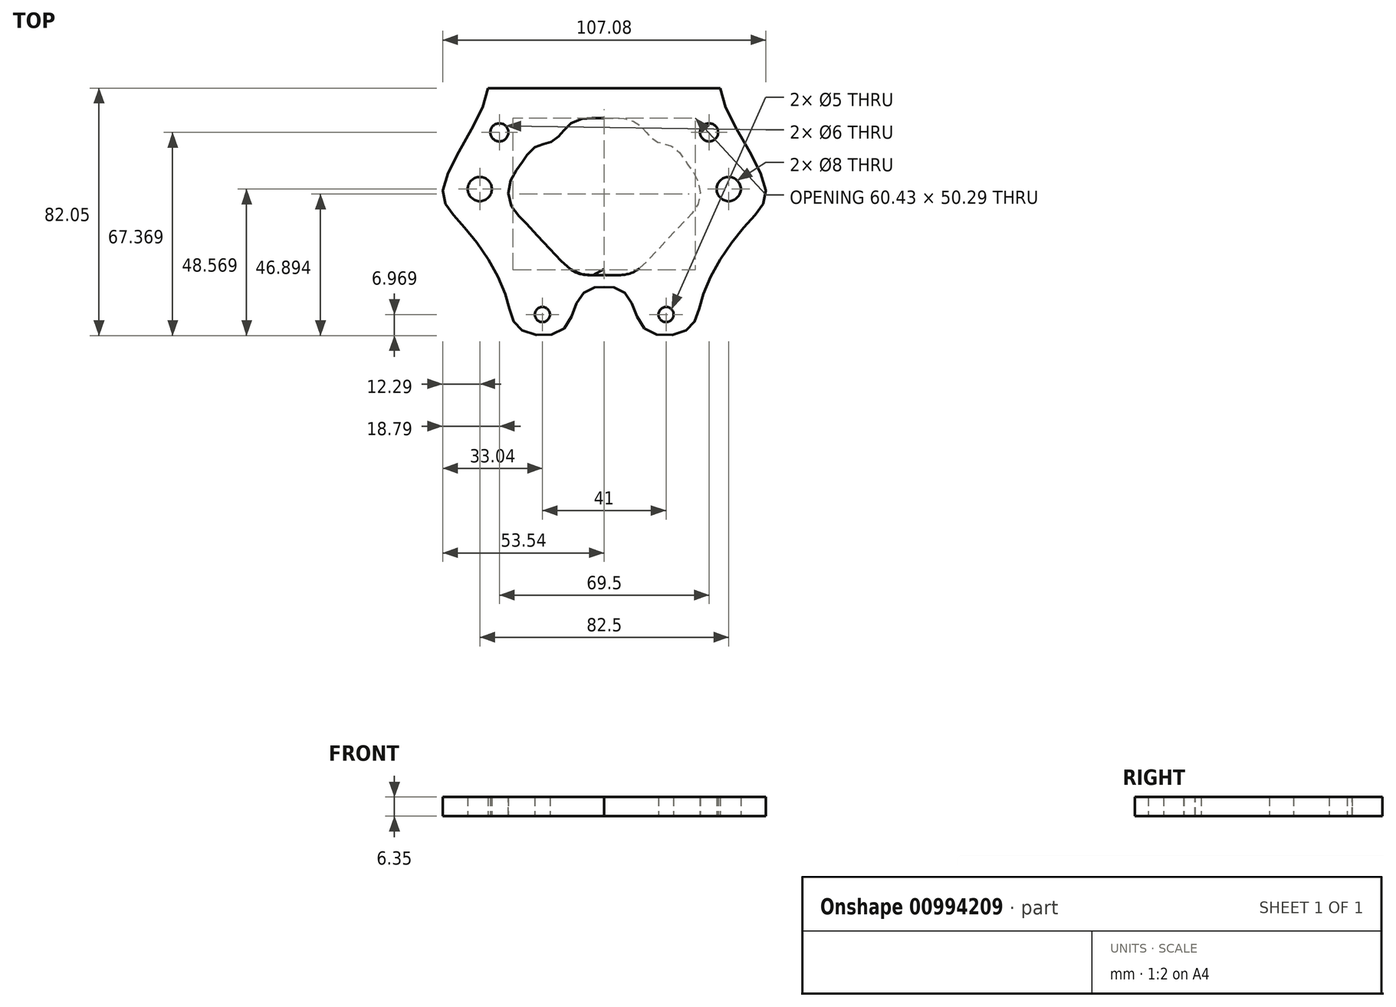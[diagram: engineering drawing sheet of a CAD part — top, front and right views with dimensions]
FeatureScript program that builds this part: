
annotation { "Feature Type Name" : "Feature", "Feature Type Description" : "" }
export const myFeature = defineFeature(function(context is Context, id is Id, definition is map)
    precondition{}
    {
        {
            var Q0;
            Q0=qCreatedBy(makeId("Top.planeOp"),FACE);
            var sketch = newSketch(context, id + "F0", { "sketchPlane" : qUnion([Q0])});
            skCircle(sketch, "E0", {"center": v(-20.5, -31.97) * mm, "radius": 2.5 * mm});
            skCircle(sketch, "E1", {"center": v(20.5, -31.97) * mm, "radius": 2.5 * mm});
            skLineSegment(sketch, "E2", {"start": v(-20.5, -31.97) * mm, "end": v(20.5, -31.97) * mm, "construction": true});
            skPoint(sketch, "E3", {"position": v(0, -31.97) * mm});
            skCircle(sketch, "E4", {"center": v(-20.5, 31.53) * mm, "radius": 2.5 * mm});
            skCircle(sketch, "E5", {"center": v(20.5, 31.53) * mm, "radius": 2.5 * mm});
            skLineSegment(sketch, "E6", {"start": v(-20.5, 31.53) * mm, "end": v(-20.5, -31.97) * mm, "construction": true});
            skLineSegment(sketch, "E7", {"start": v(20.5, 31.53) * mm, "end": v(20.5, -31.97) * mm, "construction": true});
            skLineSegment(sketch, "E8", {"start": v(-20.5, 31.53) * mm, "end": v(20.5, 31.53) * mm, "construction": true});
            skCircle(sketch, "E9", {"center": v(-34.75, 28.43) * mm, "radius": 3 * mm});
            skCircle(sketch, "E10", {"center": v(34.75, 28.43) * mm, "radius": 3 * mm});
            skLineSegment(sketch, "E11", {"start": v(-34.75, 28.43) * mm, "end": v(34.75, 28.43) * mm, "construction": true});
            skPoint(sketch, "E12", {"position": v(0, 28.43) * mm});
            skCircle(sketch, "E13", {"center": v(-41.25, 9.63) * mm, "radius": 4 * mm});
            skCircle(sketch, "E14", {"center": v(41.25, 9.63) * mm, "radius": 4 * mm});
            skLineSegment(sketch, "E15", {"start": v(-41.25, 9.63) * mm, "end": v(41.25, 9.63) * mm, "construction": true});
            skPoint(sketch, "E16", {"position": v(0, 9.63) * mm});
            skSolve(sketch);
        }
        {
            var Q0;
            Q0=qCreatedBy(makeId("Top.planeOp"),FACE);
            var sketch = newSketch(context, id + "F1", { "sketchPlane" : qUnion([Q0])});
            skPoint(sketch, "E17", {"position": v(0, 43.1) * mm});
            skPoint(sketch, "E18", {"position": v(-38.47, 43.1) * mm});
            skFitSpline(sketch, "E19", {"points": [v(-38.47, 43.1) * mm, v(-53.4, 10.03) * mm, v(-46.94, -2.29) * mm, v(-32.99, -24.7) * mm, v(-27.74, -36.86) * mm, v(-13.8, -37.01) * mm, v(-7.55, -25.5) * mm, v(0, -22.83) * mm], "startDerivative": vector(-10.62, -131.68) * mm, "endDerivative": vector(61.34, -11.47) * mm});
            skLineSegment(sketch, "E20", {"start": v(-38.47, 43.1) * mm, "end": v(0, 43.1) * mm});
            skPoint(sketch, "E21.MirrorP", {"position": v(38.47, 43.1) * mm});
            skFitSpline(sketch, "E22.MirrorCS", {"points": [v(38.47, 43.1) * mm, v(53.4, 10.03) * mm, v(46.94, -2.29) * mm, v(32.99, -24.7) * mm, v(27.74, -36.86) * mm, v(13.8, -37.01) * mm, v(7.55, -25.5) * mm, v(0, -22.83) * mm], "startDerivative": vector(10.62, -131.68) * mm, "endDerivative": vector(-61.34, -11.47) * mm});
            skLineSegment(sketch, "E23.MirrorCS", {"start": v(38.47, 43.1) * mm, "end": v(0, 43.1) * mm});
            skCircle(sketch, "E24", {"center": v(-20.5, -31.97) * mm, "radius": 2.5 * mm});
            skCircle(sketch, "E25", {"center": v(20.5, -31.97) * mm, "radius": 2.5 * mm});
            skLineSegment(sketch, "E26", {"start": v(-20.5, -31.97) * mm, "end": v(20.5, -31.97) * mm, "construction": true});
            skPoint(sketch, "E27", {"position": v(0, -31.97) * mm});
            skLineSegment(sketch, "E28", {"start": v(-20.5, 31.53) * mm, "end": v(-20.5, -31.97) * mm, "construction": true});
            skLineSegment(sketch, "E29", {"start": v(20.5, 31.53) * mm, "end": v(20.5, -31.97) * mm, "construction": true});
            skCircle(sketch, "E30", {"center": v(-34.75, 28.43) * mm, "radius": 3 * mm});
            skCircle(sketch, "E31", {"center": v(34.75, 28.43) * mm, "radius": 3 * mm});
            skLineSegment(sketch, "E32", {"start": v(-34.75, 28.43) * mm, "end": v(34.75, 28.43) * mm, "construction": true});
            skPoint(sketch, "E33", {"position": v(0, 28.43) * mm});
            skCircle(sketch, "E34", {"center": v(-41.25, 9.63) * mm, "radius": 4 * mm});
            skCircle(sketch, "E35", {"center": v(41.25, 9.63) * mm, "radius": 4 * mm});
            skLineSegment(sketch, "E36", {"start": v(-41.25, 9.63) * mm, "end": v(41.25, 9.63) * mm, "construction": true});
            skPoint(sketch, "E37", {"position": v(0, 9.63) * mm});
            skFitSpline(sketch, "E38", {"points": [v(0, 28.1) * mm, v(-5.93, 28.05) * mm, v(-8.65, 26.95) * mm, v(-10.13, 25.17) * mm, v(-15.35, 20.78) * mm, v(-20.02, 19.42) * mm, v(-21.23, 18.41) * mm, v(-23.17, 15.5) * mm, v(-26.37, 10.58) * mm, v(-26.53, 6.66) * mm, v(-24.05, 3.5) * mm, v(-16.13, -4.85) * mm, v(-9.1, -12.26) * mm, v(-6.02, -13.8) * mm, v(0, -14.01) * mm], "startDerivative": vector(-72.46, 0) * mm, "endDerivative": vector(69.37, -4.39) * mm});
            skFitSpline(sketch, "E39.MirrorCS", {"points": [v(0, 28.1) * mm, v(5.93, 28.05) * mm, v(8.65, 26.95) * mm, v(10.13, 25.17) * mm, v(15.35, 20.78) * mm, v(20.02, 19.42) * mm, v(21.23, 18.41) * mm, v(23.17, 15.5) * mm, v(26.37, 10.58) * mm, v(26.53, 6.66) * mm, v(24.05, 3.5) * mm, v(16.13, -4.85) * mm, v(9.1, -12.26) * mm, v(6.02, -13.8) * mm, v(0, -14.01) * mm], "startDerivative": vector(72.46, 0) * mm, "endDerivative": vector(-69.37, -4.39) * mm});
            skFitSpline(sketch, "E40.0", {"points": [v(0, 33.1) * mm, v(-0.3, 33.1) * mm, v(-1.01, 33.11) * mm, v(-2.24, 33.15) * mm, v(-3.36, 33.18) * mm, v(-4.3, 33.17) * mm, v(-5.04, 33.15) * mm, v(-5.67, 33.1) * mm, v(-6.2, 33.05) * mm, v(-6.6, 33) * mm, v(-7, 32.94) * mm, v(-7.54, 32.84) * mm, v(-8.2, 32.68) * mm, v(-8.96, 32.43) * mm, v(-9.7, 32.14) * mm, v(-10.42, 31.78) * mm, v(-11.11, 31.36) * mm, v(-11.66, 30.95) * mm, v(-12.08, 30.6) * mm, v(-12.46, 30.23) * mm, v(-12.87, 29.8) * mm, v(-13.24, 29.33) * mm, v(-13.52, 28.96) * mm, v(-13.74, 28.67) * mm, v(-13.9, 28.45) * mm, v(-14.03, 28.3) * mm, v(-14.17, 28.12) * mm, v(-14.38, 27.87) * mm, v(-14.77, 27.45) * mm, v(-15.34, 26.87) * mm, v(-15.96, 26.32) * mm, v(-16.45, 25.94) * mm, v(-16.81, 25.69) * mm, v(-17.14, 25.48) * mm, v(-17.39, 25.34) * mm, v(-17.55, 25.27) * mm, v(-17.68, 25.21) * mm, v(-17.82, 25.16) * mm, v(-18.03, 25.08) * mm, v(-18.31, 25) * mm, v(-18.7, 24.9) * mm, v(-19.14, 24.8) * mm, v(-19.61, 24.69) * mm, v(-20.14, 24.57) * mm, v(-20.65, 24.46) * mm, v(-21.1, 24.33) * mm, v(-21.42, 24.23) * mm, v(-21.69, 24.14) * mm, v(-21.98, 24.02) * mm, v(-22.49, 23.8) * mm, v(-23.23, 23.4) * mm, v(-24.02, 22.79) * mm, v(-24.64, 22.16) * mm, v(-25.02, 21.7) * mm, v(-25.25, 21.4) * mm, v(-25.44, 21.12) * mm, v(-25.67, 20.78) * mm, v(-25.93, 20.4) * mm, v(-26.17, 20.02) * mm, v(-26.4, 19.65) * mm, v(-26.65, 19.28) * mm, v(-26.9, 18.9) * mm, v(-27.1, 18.6) * mm, v(-27.28, 18.36) * mm, v(-27.47, 18.1) * mm, v(-27.73, 17.75) * mm, v(-28.08, 17.28) * mm, v(-28.59, 16.6) * mm, v(-29.14, 15.84) * mm, v(-29.7, 15) * mm, v(-30.11, 14.3) * mm, v(-30.52, 13.56) * mm, v(-30.84, 12.89) * mm, v(-31.07, 12.3) * mm, v(-31.28, 11.71) * mm, v(-31.5, 10.96) * mm, v(-31.69, 10.05) * mm, v(-31.84, 8.83) * mm, v(-31.83, 7.6) * mm, v(-31.64, 6.36) * mm, v(-31.42, 5.45) * mm, v(-31.09, 4.54) * mm, v(-30.68, 3.7) * mm, v(-30.22, 2.95) * mm, v(-29.6, 2.09) * mm, v(-28.97, 1.39) * mm, v(-28.39, 0.78) * mm, v(-28.03, 0.42) * mm, v(-27.75, 0.14) * mm, v(-27.47, -0.14) * mm, v(-27.11, -0.5) * mm, v(-26.64, -0.98) * mm, v(-25.99, -1.65) * mm, v(-25.1, -2.57) * mm, v(-23.98, -3.75) * mm, v(-22.8, -5) * mm, v(-21.6, -6.3) * mm, v(-20.38, -7.6) * mm, v(-19.18, -8.93) * mm, v(-17.98, -10.25) * mm, v(-16.8, -11.53) * mm, v(-15.67, -12.77) * mm, v(-14.57, -13.93) * mm, v(-13.68, -14.82) * mm, v(-12.98, -15.48) * mm, v(-12.46, -15.96) * mm, v(-11.92, -16.41) * mm, v(-11.34, -16.87) * mm, v(-10.68, -17.32) * mm, v(-9.95, -17.74) * mm, v(-9.15, -18.1) * mm, v(-8.32, -18.4) * mm, v(-7.63, -18.58) * mm, v(-7.08, -18.7) * mm, v(-6.54, -18.78) * mm, v(-5.89, -18.86) * mm, v(-4.9, -18.93) * mm, v(-3.71, -18.96) * mm, v(-2.38, -18.96) * mm, v(-1.2, -18.97) * mm, v(-0.56, -18.99) * mm, v(-0.32, -19) * mm, v(0, 33.1) * mm]});
            skFitSpline(sketch, "E40.1", {"points": [v(0, 33.1) * mm, v(0.3, 33.1) * mm, v(1.01, 33.11) * mm, v(2.24, 33.15) * mm, v(3.36, 33.18) * mm, v(4.3, 33.17) * mm, v(5.04, 33.15) * mm, v(5.67, 33.1) * mm, v(6.2, 33.05) * mm, v(6.6, 33) * mm, v(7, 32.94) * mm, v(7.54, 32.84) * mm, v(8.2, 32.68) * mm, v(8.96, 32.43) * mm, v(9.7, 32.14) * mm, v(10.42, 31.78) * mm, v(11.11, 31.36) * mm, v(11.66, 30.95) * mm, v(12.08, 30.6) * mm, v(12.46, 30.23) * mm, v(12.87, 29.8) * mm, v(13.24, 29.33) * mm, v(13.52, 28.96) * mm, v(13.74, 28.67) * mm, v(13.9, 28.45) * mm, v(14.03, 28.3) * mm, v(14.17, 28.12) * mm, v(14.38, 27.87) * mm, v(14.77, 27.45) * mm, v(15.34, 26.87) * mm, v(15.96, 26.32) * mm, v(16.45, 25.94) * mm, v(16.81, 25.69) * mm, v(17.14, 25.48) * mm, v(17.39, 25.34) * mm, v(17.55, 25.27) * mm, v(17.68, 25.21) * mm, v(17.82, 25.16) * mm, v(18.03, 25.08) * mm, v(18.31, 25) * mm, v(18.7, 24.9) * mm, v(19.14, 24.8) * mm, v(19.61, 24.69) * mm, v(20.14, 24.57) * mm, v(20.65, 24.46) * mm, v(21.1, 24.33) * mm, v(21.42, 24.23) * mm, v(21.69, 24.14) * mm, v(21.98, 24.02) * mm, v(22.49, 23.8) * mm, v(23.23, 23.4) * mm, v(24.02, 22.79) * mm, v(24.64, 22.16) * mm, v(25.02, 21.7) * mm, v(25.25, 21.4) * mm, v(25.44, 21.12) * mm, v(25.67, 20.78) * mm, v(25.93, 20.4) * mm, v(26.17, 20.02) * mm, v(26.4, 19.65) * mm, v(26.65, 19.28) * mm, v(26.9, 18.9) * mm, v(27.1, 18.6) * mm, v(27.28, 18.36) * mm, v(27.47, 18.1) * mm, v(27.73, 17.75) * mm, v(28.08, 17.28) * mm, v(28.59, 16.6) * mm, v(29.14, 15.84) * mm, v(29.7, 15) * mm, v(30.11, 14.3) * mm, v(30.52, 13.56) * mm, v(30.84, 12.89) * mm, v(31.07, 12.3) * mm, v(31.28, 11.71) * mm, v(31.5, 10.96) * mm, v(31.69, 10.05) * mm, v(31.84, 8.83) * mm, v(31.83, 7.6) * mm, v(31.64, 6.36) * mm, v(31.42, 5.45) * mm, v(31.09, 4.54) * mm, v(30.68, 3.7) * mm, v(30.22, 2.95) * mm, v(29.6, 2.09) * mm, v(28.97, 1.39) * mm, v(28.39, 0.78) * mm, v(28.03, 0.42) * mm, v(27.75, 0.14) * mm, v(27.47, -0.14) * mm, v(27.11, -0.5) * mm, v(26.64, -0.98) * mm, v(25.99, -1.65) * mm, v(25.1, -2.57) * mm, v(23.98, -3.75) * mm, v(22.8, -5) * mm, v(21.6, -6.3) * mm, v(20.38, -7.6) * mm, v(19.18, -8.93) * mm, v(17.98, -10.25) * mm, v(16.8, -11.53) * mm, v(15.67, -12.77) * mm, v(14.57, -13.93) * mm, v(13.68, -14.82) * mm, v(12.98, -15.48) * mm, v(12.46, -15.96) * mm, v(11.92, -16.41) * mm, v(11.34, -16.87) * mm, v(10.68, -17.32) * mm, v(9.95, -17.74) * mm, v(9.15, -18.1) * mm, v(8.32, -18.4) * mm, v(7.63, -18.58) * mm, v(7.08, -18.7) * mm, v(6.54, -18.78) * mm, v(5.89, -18.86) * mm, v(4.9, -18.93) * mm, v(3.71, -18.96) * mm, v(2.38, -18.96) * mm, v(1.2, -18.97) * mm, v(0.56, -18.99) * mm, v(0.32, -19) * mm, v(0, 33.1) * mm]});
            skFitSpline(sketch, "E41.0", {"points": [v(0, 31.6) * mm, v(-0.33, 31.6) * mm, v(-1.06, 31.61) * mm, v(-2.29, 31.65) * mm, v(-3.38, 31.68) * mm, v(-4.28, 31.67) * mm, v(-4.97, 31.65) * mm, v(-5.67, 31.6) * mm, v(-6.26, 31.54) * mm, v(-6.74, 31.46) * mm, v(-7.21, 31.37) * mm, v(-7.79, 31.23) * mm, v(-8.45, 31.02) * mm, v(-9.09, 30.76) * mm, v(-9.7, 30.46) * mm, v(-10.28, 30.11) * mm, v(-10.73, 29.78) * mm, v(-11.08, 29.48) * mm, v(-11.4, 29.18) * mm, v(-11.73, 28.81) * mm, v(-12.16, 28.28) * mm, v(-12.47, 27.86) * mm, v(-12.71, 27.54) * mm, v(-12.86, 27.35) * mm, v(-13.02, 27.15) * mm, v(-13.26, 26.88) * mm, v(-13.68, 26.4) * mm, v(-14.3, 25.78) * mm, v(-15, 25.17) * mm, v(-15.56, 24.74) * mm, v(-15.98, 24.44) * mm, v(-16.38, 24.18) * mm, v(-16.7, 24.01) * mm, v(-16.93, 23.9) * mm, v(-17.17, 23.8) * mm, v(-17.49, 23.68) * mm, v(-17.9, 23.55) * mm, v(-18.35, 23.43) * mm, v(-18.81, 23.32) * mm, v(-19.3, 23.22) * mm, v(-19.82, 23.1) * mm, v(-20.37, 22.98) * mm, v(-20.98, 22.8) * mm, v(-21.7, 22.52) * mm, v(-22.4, 22.13) * mm, v(-23.03, 21.65) * mm, v(-23.53, 21.16) * mm, v(-23.9, 20.7) * mm, v(-24.17, 20.32) * mm, v(-24.43, 19.95) * mm, v(-24.67, 19.58) * mm, v(-24.9, 19.21) * mm, v(-25.15, 18.83) * mm, v(-25.4, 18.45) * mm, v(-25.65, 18.07) * mm, v(-25.88, 17.74) * mm, v(-26.06, 17.48) * mm, v(-26.26, 17.21) * mm, v(-26.53, 16.85) * mm, v(-26.88, 16.38) * mm, v(-27.38, 15.7) * mm, v(-28.04, 14.8) * mm, v(-28.7, 13.78) * mm, v(-29.18, 12.88) * mm, v(-29.52, 12.16) * mm, v(-29.82, 11.38) * mm, v(-30.05, 10.6) * mm, v(-30.2, 9.81) * mm, v(-30.33, 8.75) * mm, v(-30.32, 7.43) * mm, v(-30.07, 6.14) * mm, v(-29.7, 5.13) * mm, v(-29.25, 4.19) * mm, v(-28.57, 3.2) * mm, v(-27.73, 2.25) * mm, v(-27.1, 1.62) * mm, v(-26.69, 1.2) * mm, v(-26.4, 0.92) * mm, v(-26.04, 0.55) * mm, v(-25.57, 0.07) * mm, v(-24.9, -0.61) * mm, v(-24.02, -1.53) * mm, v(-22.9, -2.72) * mm, v(-21.32, -4.4) * mm, v(-19.68, -6.15) * mm, v(-18.07, -7.92) * mm, v(-16.87, -9.24) * mm, v(-15.7, -10.52) * mm, v(-14.57, -11.75) * mm, v(-13.49, -12.89) * mm, v(-12.63, -13.75) * mm, v(-11.96, -14.39) * mm, v(-11.47, -14.83) * mm, v(-10.97, -15.25) * mm, v(-10.45, -15.66) * mm, v(-9.88, -16.05) * mm, v(-9.05, -16.53) * mm, v(-8.12, -16.9) * mm, v(-7.17, -17.15) * mm, v(-6.21, -17.32) * mm, v(-5.06, -17.42) * mm, v(-3.7, -17.46) * mm, v(-2.38, -17.46) * mm, v(-1.18, -17.47) * mm, v(-0.5, -17.5) * mm, v(-0.22, -17.5) * mm, v(0, 31.6) * mm]});
            skFitSpline(sketch, "E41.1", {"points": [v(0, 31.6) * mm, v(0.33, 31.6) * mm, v(1.06, 31.61) * mm, v(2.29, 31.65) * mm, v(3.38, 31.68) * mm, v(4.28, 31.67) * mm, v(4.97, 31.65) * mm, v(5.67, 31.6) * mm, v(6.26, 31.54) * mm, v(6.74, 31.46) * mm, v(7.21, 31.37) * mm, v(7.79, 31.23) * mm, v(8.45, 31.02) * mm, v(9.09, 30.76) * mm, v(9.7, 30.46) * mm, v(10.28, 30.11) * mm, v(10.73, 29.78) * mm, v(11.08, 29.48) * mm, v(11.4, 29.18) * mm, v(11.73, 28.81) * mm, v(12.16, 28.28) * mm, v(12.47, 27.86) * mm, v(12.71, 27.54) * mm, v(12.86, 27.35) * mm, v(13.02, 27.15) * mm, v(13.26, 26.88) * mm, v(13.68, 26.4) * mm, v(14.3, 25.78) * mm, v(15, 25.17) * mm, v(15.56, 24.74) * mm, v(15.98, 24.44) * mm, v(16.38, 24.18) * mm, v(16.7, 24.01) * mm, v(16.93, 23.9) * mm, v(17.17, 23.8) * mm, v(17.49, 23.68) * mm, v(17.9, 23.55) * mm, v(18.35, 23.43) * mm, v(18.81, 23.32) * mm, v(19.3, 23.22) * mm, v(19.82, 23.1) * mm, v(20.37, 22.98) * mm, v(20.98, 22.8) * mm, v(21.7, 22.52) * mm, v(22.4, 22.13) * mm, v(23.03, 21.65) * mm, v(23.53, 21.16) * mm, v(23.9, 20.7) * mm, v(24.17, 20.32) * mm, v(24.43, 19.95) * mm, v(24.67, 19.58) * mm, v(24.9, 19.21) * mm, v(25.15, 18.83) * mm, v(25.4, 18.45) * mm, v(25.65, 18.07) * mm, v(25.88, 17.74) * mm, v(26.06, 17.48) * mm, v(26.26, 17.21) * mm, v(26.53, 16.85) * mm, v(26.88, 16.38) * mm, v(27.38, 15.7) * mm, v(28.04, 14.8) * mm, v(28.7, 13.78) * mm, v(29.18, 12.88) * mm, v(29.52, 12.16) * mm, v(29.82, 11.38) * mm, v(30.05, 10.6) * mm, v(30.2, 9.81) * mm, v(30.33, 8.75) * mm, v(30.32, 7.43) * mm, v(30.07, 6.14) * mm, v(29.7, 5.13) * mm, v(29.25, 4.19) * mm, v(28.57, 3.2) * mm, v(27.73, 2.25) * mm, v(27.1, 1.62) * mm, v(26.69, 1.2) * mm, v(26.4, 0.92) * mm, v(26.04, 0.55) * mm, v(25.57, 0.07) * mm, v(24.9, -0.61) * mm, v(24.02, -1.53) * mm, v(22.9, -2.72) * mm, v(21.32, -4.4) * mm, v(19.68, -6.15) * mm, v(18.07, -7.92) * mm, v(16.87, -9.24) * mm, v(15.7, -10.52) * mm, v(14.57, -11.75) * mm, v(13.49, -12.89) * mm, v(12.63, -13.75) * mm, v(11.96, -14.39) * mm, v(11.47, -14.83) * mm, v(10.97, -15.25) * mm, v(10.45, -15.66) * mm, v(9.88, -16.05) * mm, v(9.05, -16.53) * mm, v(8.12, -16.9) * mm, v(7.17, -17.15) * mm, v(6.21, -17.32) * mm, v(5.06, -17.42) * mm, v(3.7, -17.46) * mm, v(2.38, -17.46) * mm, v(1.18, -17.47) * mm, v(0.5, -17.5) * mm, v(0.22, -17.5) * mm, v(0, 31.6) * mm]});
            skFitSpline(sketch, "E42.0", {"points": [v(0, 31.8) * mm, v(-0.33, 31.8) * mm, v(-1.05, 31.81) * mm, v(-2.28, 31.85) * mm, v(-3.38, 31.88) * mm, v(-4.28, 31.87) * mm, v(-4.98, 31.85) * mm, v(-5.68, 31.8) * mm, v(-6.29, 31.74) * mm, v(-6.78, 31.66) * mm, v(-7.26, 31.57) * mm, v(-7.84, 31.42) * mm, v(-8.52, 31.2) * mm, v(-9.17, 30.95) * mm, v(-9.8, 30.64) * mm, v(-10.39, 30.28) * mm, v(-10.86, 29.93) * mm, v(-11.21, 29.63) * mm, v(-11.54, 29.32) * mm, v(-11.88, 28.94) * mm, v(-12.21, 28.54) * mm, v(-12.48, 28.2) * mm, v(-12.7, 27.9) * mm, v(-12.87, 27.66) * mm, v(-13.02, 27.48) * mm, v(-13.18, 27.28) * mm, v(-13.4, 27.01) * mm, v(-13.83, 26.55) * mm, v(-14.44, 25.93) * mm, v(-15.12, 25.33) * mm, v(-15.68, 24.9) * mm, v(-16.09, 24.6) * mm, v(-16.48, 24.36) * mm, v(-16.79, 24.19) * mm, v(-17, 24.08) * mm, v(-17.24, 23.98) * mm, v(-17.55, 23.87) * mm, v(-17.96, 23.74) * mm, v(-18.4, 23.63) * mm, v(-18.86, 23.52) * mm, v(-19.34, 23.42) * mm, v(-19.86, 23.3) * mm, v(-20.42, 23.17) * mm, v(-20.9, 23.04) * mm, v(-21.24, 22.91) * mm, v(-21.48, 22.82) * mm, v(-21.9, 22.64) * mm, v(-22.51, 22.3) * mm, v(-23.16, 21.8) * mm, v(-23.68, 21.29) * mm, v(-24, 20.9) * mm, v(-24.2, 20.63) * mm, v(-24.38, 20.38) * mm, v(-24.6, 20.06) * mm, v(-24.84, 19.7) * mm, v(-25.08, 19.32) * mm, v(-25.32, 18.94) * mm, v(-25.56, 18.56) * mm, v(-25.82, 18.18) * mm, v(-26.04, 17.86) * mm, v(-26.22, 17.6) * mm, v(-26.42, 17.33) * mm, v(-26.69, 16.97) * mm, v(-27.04, 16.5) * mm, v(-27.54, 15.83) * mm, v(-28.2, 14.91) * mm, v(-28.86, 13.88) * mm, v(-29.36, 12.97) * mm, v(-29.7, 12.24) * mm, v(-30, 11.45) * mm, v(-30.24, 10.65) * mm, v(-30.4, 9.84) * mm, v(-30.53, 8.76) * mm, v(-30.52, 7.41) * mm, v(-30.26, 6.09) * mm, v(-29.89, 5.05) * mm, v(-29.42, 4.09) * mm, v(-28.73, 3.07) * mm, v(-27.87, 2.11) * mm, v(-27.25, 1.48) * mm, v(-26.83, 1.06) * mm, v(-26.55, 0.78) * mm, v(-26.18, 0.4) * mm, v(-25.71, -0.07) * mm, v(-25.05, -0.75) * mm, v(-24.17, -1.67) * mm, v(-23.04, -2.86) * mm, v(-21.46, -4.53) * mm, v(-19.83, -6.29) * mm, v(-18.21, -8.05) * mm, v(-17.02, -9.37) * mm, v(-15.85, -10.66) * mm, v(-14.72, -11.88) * mm, v(-13.63, -13.03) * mm, v(-12.77, -13.9) * mm, v(-12.1, -14.53) * mm, v(-11.6, -14.98) * mm, v(-11.1, -15.4) * mm, v(-10.57, -15.82) * mm, v(-9.99, -16.22) * mm, v(-9.14, -16.7) * mm, v(-8.18, -17.1) * mm, v(-7.21, -17.35) * mm, v(-6.24, -17.52) * mm, v(-5.07, -17.62) * mm, v(-3.7, -17.66) * mm, v(-2.38, -17.66) * mm, v(-1.18, -17.67) * mm, v(-0.51, -17.69) * mm, v(-0.23, -17.7) * mm, v(0, 31.8) * mm]});
            skFitSpline(sketch, "E42.1", {"points": [v(0, 31.8) * mm, v(0.33, 31.8) * mm, v(1.05, 31.81) * mm, v(2.28, 31.85) * mm, v(3.38, 31.88) * mm, v(4.28, 31.87) * mm, v(4.98, 31.85) * mm, v(5.68, 31.8) * mm, v(6.29, 31.74) * mm, v(6.78, 31.66) * mm, v(7.26, 31.57) * mm, v(7.84, 31.42) * mm, v(8.52, 31.2) * mm, v(9.17, 30.95) * mm, v(9.8, 30.64) * mm, v(10.39, 30.28) * mm, v(10.86, 29.93) * mm, v(11.21, 29.63) * mm, v(11.54, 29.32) * mm, v(11.88, 28.94) * mm, v(12.21, 28.54) * mm, v(12.48, 28.2) * mm, v(12.7, 27.9) * mm, v(12.87, 27.66) * mm, v(13.02, 27.48) * mm, v(13.18, 27.28) * mm, v(13.4, 27.01) * mm, v(13.83, 26.55) * mm, v(14.44, 25.93) * mm, v(15.12, 25.33) * mm, v(15.68, 24.9) * mm, v(16.09, 24.6) * mm, v(16.48, 24.36) * mm, v(16.79, 24.19) * mm, v(17, 24.08) * mm, v(17.24, 23.98) * mm, v(17.55, 23.87) * mm, v(17.96, 23.74) * mm, v(18.4, 23.63) * mm, v(18.86, 23.52) * mm, v(19.34, 23.42) * mm, v(19.86, 23.3) * mm, v(20.42, 23.17) * mm, v(20.9, 23.04) * mm, v(21.24, 22.91) * mm, v(21.48, 22.82) * mm, v(21.9, 22.64) * mm, v(22.51, 22.3) * mm, v(23.16, 21.8) * mm, v(23.68, 21.29) * mm, v(24, 20.9) * mm, v(24.2, 20.63) * mm, v(24.38, 20.38) * mm, v(24.6, 20.06) * mm, v(24.84, 19.7) * mm, v(25.08, 19.32) * mm, v(25.32, 18.94) * mm, v(25.56, 18.56) * mm, v(25.82, 18.18) * mm, v(26.04, 17.86) * mm, v(26.22, 17.6) * mm, v(26.42, 17.33) * mm, v(26.69, 16.97) * mm, v(27.04, 16.5) * mm, v(27.54, 15.83) * mm, v(28.2, 14.91) * mm, v(28.86, 13.88) * mm, v(29.36, 12.97) * mm, v(29.7, 12.24) * mm, v(30, 11.45) * mm, v(30.24, 10.65) * mm, v(30.4, 9.84) * mm, v(30.53, 8.76) * mm, v(30.52, 7.41) * mm, v(30.26, 6.09) * mm, v(29.89, 5.05) * mm, v(29.42, 4.09) * mm, v(28.73, 3.07) * mm, v(27.87, 2.11) * mm, v(27.25, 1.48) * mm, v(26.83, 1.06) * mm, v(26.55, 0.78) * mm, v(26.18, 0.4) * mm, v(25.71, -0.07) * mm, v(25.05, -0.75) * mm, v(24.17, -1.67) * mm, v(23.04, -2.86) * mm, v(21.46, -4.53) * mm, v(19.83, -6.29) * mm, v(18.21, -8.05) * mm, v(17.02, -9.37) * mm, v(15.85, -10.66) * mm, v(14.72, -11.88) * mm, v(13.63, -13.03) * mm, v(12.77, -13.9) * mm, v(12.1, -14.53) * mm, v(11.6, -14.98) * mm, v(11.1, -15.4) * mm, v(10.57, -15.82) * mm, v(9.99, -16.22) * mm, v(9.14, -16.7) * mm, v(8.18, -17.1) * mm, v(7.21, -17.35) * mm, v(6.24, -17.52) * mm, v(5.07, -17.62) * mm, v(3.7, -17.66) * mm, v(2.38, -17.66) * mm, v(1.18, -17.67) * mm, v(0.51, -17.69) * mm, v(0.23, -17.7) * mm, v(0, 31.8) * mm]});
            skSolve(sketch);
        }
        {
            var Q0;
            Q0=makeQuery(id+"F1.imprint","IMPRINT",FACE,{"disambiguationData":[TD([[makeQuery(id+"F1.imprint","IMPRINT",EDGE,{"derivedFrom":sQuery(id+"F1.wireOp",EDGE,"E19")}),1.0]])]});
            extrude(context, id + "F2", {"entities" : qUnion([Q0]), "depth" : 6.35 * mm, "offsetDistance" : 25 * mm});
        }
    });
